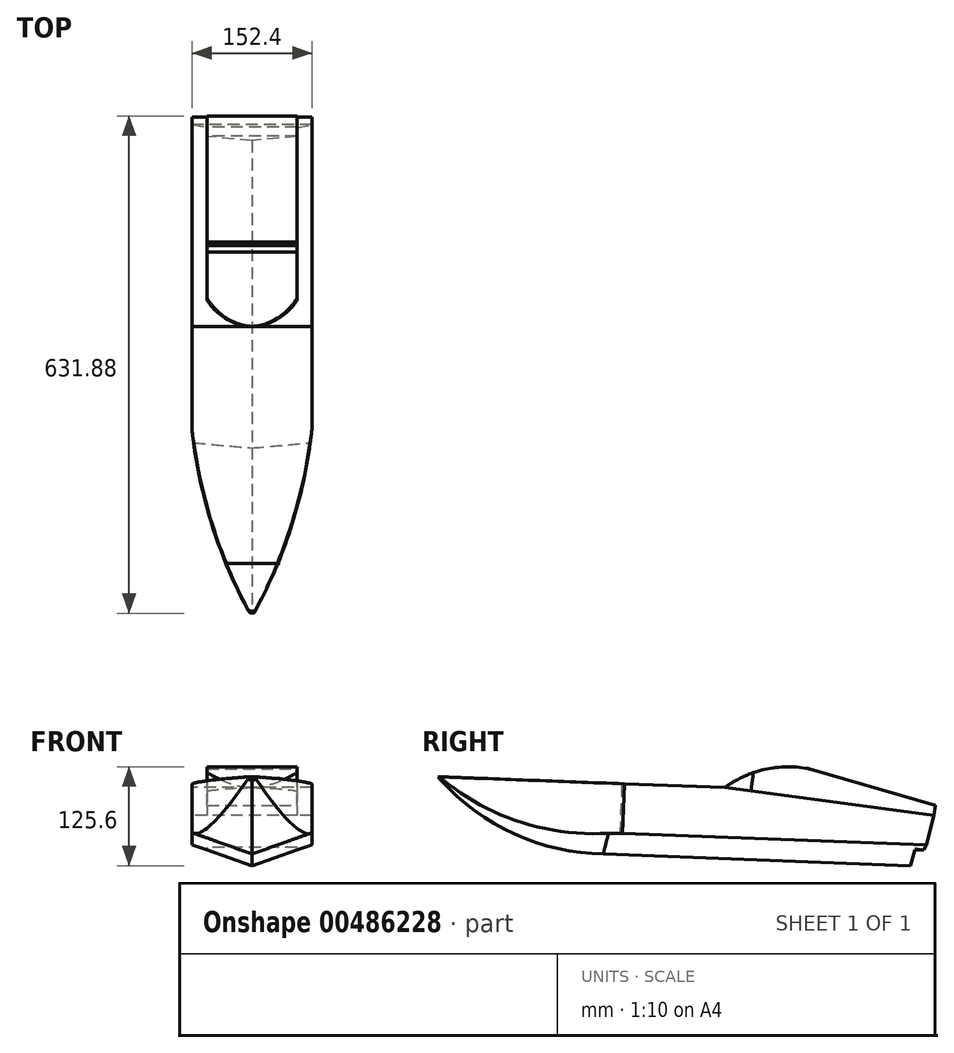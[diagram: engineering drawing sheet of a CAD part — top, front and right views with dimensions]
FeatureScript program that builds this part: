
annotation { "Feature Type Name" : "Feature", "Feature Type Description" : "" }
export const myFeature = defineFeature(function(context is Context, id is Id, definition is map)
    precondition{}
    {
        {
            var Q0;
            Q0=qCreatedBy(makeId("Right.planeOp"),FACE);
            var sketch = newSketch(context, id + "F0", { "sketchPlane" : qUnion([Q0])});
            skLineSegment(sketch, "E0", {"start": v(-294.84, 31.95) * mm, "end": v(70.05, 18.1) * mm});
            skLineSegment(sketch, "E1", {"start": v(70.05, 18.1) * mm, "end": v(335.9, -17.4) * mm});
            skLineSegment(sketch, "E2", {"start": v(335.9, -17.4) * mm, "end": v(326.2, -54.44) * mm});
            skLineSegment(sketch, "E3", {"start": v(326.2, -54.44) * mm, "end": v(73.83, -35.78) * mm});
            skArc(sketch, "E4", {"start": v(-294.84, 31.95) * mm, "mid": v(-201.79, -39.18) * mm, "end": v(-87.88, -66.47) * mm});
            skArc(sketch, "E5", {"start": v(-281.12, 17.08) * mm, "mid": v(-104.62, -15.92) * mm, "end": v(73.83, -35.78) * mm});
            skLineSegment(sketch, "E6", {"start": v(-87.88, -66.47) * mm, "end": v(312.96, -81.69) * mm});
            skLineSegment(sketch, "E7", {"start": v(326.2, -54.44) * mm, "end": v(312.96, -81.69) * mm});
            skLineSegment(sketch, "E8", {"start": v(-294.84, 31.95) * mm, "end": v(-379.88, 131.03) * mm});
            skLineSegment(sketch, "E9", {"start": v(-379.88, 131.03) * mm, "end": v(-230.86, 29.52) * mm});
            skSolve(sketch);
        }
        {
            var Q0;
            Q0 = qSketchRegion(id + "F0", true);
            extrude(context, id + "F1", {"entities" : qUnion([Q0]), "depth" : 152.4 * mm, "offsetDistance" : 25.4 * mm});
        }
        {
            var Q0;
            Q0=makeQuery(id+"F1.opExtrude","SWEPT_FACE",FACE,{"disambiguationData":[OSD([sQuery(id+"F0.wireOp",EDGE,"E2")])]});
            var sketch = newSketch(context, id + "F2", { "sketchPlane" : qUnion([Q0])});
            skLineSegment(sketch, "E10", {"start": v(-76.2, 29.96) * mm, "end": v(-76.2, 11.3) * mm, "construction": true});
            skLineSegment(sketch, "E11", {"start": v(-76.2, 11.3) * mm, "end": v(-76.2, 7.51) * mm, "construction": true});
            skLineSegment(sketch, "E12", {"start": v(0, 7.51) * mm, "end": v(0, 29.96) * mm});
            skLineSegment(sketch, "E13", {"start": v(-152.4, 29.96) * mm, "end": v(-76.2, 29.96) * mm});
            skLineSegment(sketch, "E14", {"start": v(0, 29.96) * mm, "end": v(-76.2, 29.96) * mm});
            skLineSegment(sketch, "E15", {"start": v(-76.2, 29.96) * mm, "end": v(-76.2, 7.51) * mm});
            skLineSegment(sketch, "E16", {"start": v(0, 29.96) * mm, "end": v(0, 18.74) * mm});
            skLineSegment(sketch, "E17", {"start": v(0, 29.96) * mm, "end": v(45.97, -2.77) * mm});
            skLineSegment(sketch, "E18", {"start": v(45.97, -2.77) * mm, "end": v(-180.85, -2.77) * mm});
            skLineSegment(sketch, "E19", {"start": v(-180.85, -2.77) * mm, "end": v(-152.4, 29.96) * mm});
            skLineSegment(sketch, "E20", {"start": v(-180.85, -2.77) * mm, "end": v(-273.96, -108.66) * mm});
            skLineSegment(sketch, "E21", {"start": v(-273.96, -108.66) * mm, "end": v(130.47, -108.66) * mm});
            skLineSegment(sketch, "E22", {"start": v(130.47, -108.66) * mm, "end": v(45.97, -2.77) * mm});
            skLineSegment(sketch, "E23", {"start": v(-152.4, 29.96) * mm, "end": v(-76.2, 1.98) * mm});
            skLineSegment(sketch, "E24", {"start": v(-76.2, 1.98) * mm, "end": v(0, 29.96) * mm});
            skSolve(sketch);
        }
        {
            var Q0;
            Q0=makeQuery(id+"F1.opExtrude","CAP_FACE",FACE,{"disambiguationData":[OSD([sQuery(id+"F0.wireOp",EDGE,"E0"),sQuery(id+"F0.wireOp",EDGE,"E1"),sQuery(id+"F0.wireOp",EDGE,"E2"),sQuery(id+"F0.wireOp",EDGE,"E4"),sQuery(id+"F0.wireOp",EDGE,"E6"),sQuery(id+"F0.wireOp",EDGE,"E7")])],"isStart":true});
            var sketch = newSketch(context, id + "F3", { "sketchPlane" : qUnion([Q0])});
            skLineSegment(sketch, "E25", {"start": v(-326.2, -54.44) * mm, "end": v(-60.2, -32.43) * mm});
            skArc(sketch, "E26", {"start": v(-60.2, -32.43) * mm, "mid": v(114.76, -14.87) * mm, "end": v(286.54, 22.7) * mm});
            skLineSegment(sketch, "E27", {"start": v(286.54, 22.7) * mm, "end": v(364.94, 59.76) * mm});
            skSolve(sketch);
        }
        {
            var Q0;
            Q0=makeQuery(id+"F2.imprint","IMPRINT",FACE,{"disambiguationData":[TD([[makeQuery(id+"F2.imprint","IMPRINT",EDGE,{"derivedFrom":sQuery(id+"F2.wireOp",EDGE,"E17")}),-1.0]])]});
            var Q1;
            Q1=makeQuery(id+"F2.imprint","IMPRINT",FACE,{"disambiguationData":[TD([[makeQuery(id+"F2.imprint","IMPRINT",EDGE,{"derivedFrom":sQuery(id+"F2.wireOp",EDGE,"E18")}),1.0]])]});
            var Q2;
            Q2=makeQuery(id+"F1.opExtrude","CAP_EDGE",EDGE,{"disambiguationData":[OSD([sQuery(id+"F0.wireOp",EDGE,"E8")])],"isStart":false});
            var Q3;
            Q3=makeQuery(id+"F1.opExtrude","CAP_EDGE",EDGE,{"disambiguationData":[OSD([sQuery(id+"F0.wireOp",EDGE,"E4")])],"isStart":false});
            var Q4;
            Q4=makeQuery(id+"F1.opExtrude","CAP_EDGE",EDGE,{"disambiguationData":[OSD([sQuery(id+"F0.wireOp",EDGE,"E6")])],"isStart":false});
            sweep(context, id + "F4", {"operationType" : NewBodyOperationType.REMOVE, "profiles" : qUnion([Q0, Q1]), "path" : qUnion([Q2, Q3, Q4])});
        }
        {
            var Q0;
            Q0=makeQuery(id+"F1.opExtrude","CAP_FACE",FACE,{"disambiguationData":[OSD([sQuery(id+"F0.wireOp",EDGE,"E0"),sQuery(id+"F0.wireOp",EDGE,"E1"),sQuery(id+"F0.wireOp",EDGE,"E2"),sQuery(id+"F0.wireOp",EDGE,"E4"),sQuery(id+"F0.wireOp",EDGE,"E6"),sQuery(id+"F0.wireOp",EDGE,"E7")])],"isStart":false});
            var sketch = newSketch(context, id + "F5", { "sketchPlane" : qUnion([Q0])});
            skArc(sketch, "E28", {"start": v(-386.63, 122.11) * mm, "mid": v(-246.1, 14.63) * mm, "end": v(-77.53, -39.12) * mm});
            skLineSegment(sketch, "E29", {"start": v(-230.86, 29.52) * mm, "end": v(-280, 33.98) * mm});
            skLineSegment(sketch, "E30", {"start": v(-280, 33.98) * mm, "end": v(-230.86, 29.52) * mm});
            skLineSegment(sketch, "E31", {"start": v(-230.86, 29.52) * mm, "end": v(-226.23, 151.46) * mm});
            skLineSegment(sketch, "E32", {"start": v(-226.23, 151.46) * mm, "end": v(-406.8, 151.46) * mm});
            skLineSegment(sketch, "E33", {"start": v(-406.8, 151.46) * mm, "end": v(-386.63, 122.11) * mm});
            skLineSegment(sketch, "E34", {"start": v(-280, 33.98) * mm, "end": v(-323.7, 40.75) * mm});
            skLineSegment(sketch, "E35", {"start": v(-323.7, 40.75) * mm, "end": v(-320.42, 61.87) * mm});
            skSolve(sketch);
        }
        {
            var Q0;
            Q0 = qSketchRegion(id + "F5", true);
            extrude(context, id + "F6", {"entities" : qUnion([Q0]), "operationType" : NewBodyOperationType.REMOVE, "oppositeDirection" : true, "depth" : 584.2 * mm, "offsetDistance" : 25.4 * mm});
        }
        {
            var Q0;
            Q0=makeQuery(id+"F1.opExtrude","SWEPT_FACE",FACE,{"disambiguationData":[OSD([sQuery(id+"F0.wireOp",EDGE,"E0")])]});
            var sketch = newSketch(context, id + "F7", { "sketchPlane" : qUnion([Q0])});
            skArc(sketch, "E36", {"start": v(76.04, -299.98) * mm, "mid": v(126.16, -182.86) * mm, "end": v(152.4, -58.2) * mm});
            skLineSegment(sketch, "E37", {"start": v(76.04, -299.98) * mm, "end": v(76.04, -160.68) * mm, "construction": true});
            skArc(sketch, "E38.MirrorCS", {"start": v(76.04, -299.98) * mm, "mid": v(25.92, -182.86) * mm, "end": v(-0.32, -58.2) * mm});
            skLineSegment(sketch, "E39", {"start": v(152.4, -58.2) * mm, "end": v(161.27, -70.32) * mm});
            skLineSegment(sketch, "E40", {"start": v(152.4, -58.2) * mm, "end": v(307.31, -259.52) * mm});
            skLineSegment(sketch, "E41", {"start": v(307.31, -259.52) * mm, "end": v(76.04, -299.98) * mm});
            skLineSegment(sketch, "E42", {"start": v(76.04, -299.98) * mm, "end": v(-128.98, -291.66) * mm});
            skLineSegment(sketch, "E43", {"start": v(-128.98, -291.66) * mm, "end": v(-0.32, -58.2) * mm});
            skSolve(sketch);
        }
        {
            var Q0;
            Q0 = qSketchRegion(id + "F7", true);
            extrude(context, id + "F8", {"entities" : qUnion([Q0]), "operationType" : NewBodyOperationType.REMOVE, "oppositeDirection" : true, "depth" : 508 * mm, "offsetDistance" : 25.4 * mm});
        }
        {
            var Q0;
            Q0=makeQuery(id+"F8.boolean.opBoolean","COPY",FACE,{"derivedFrom":makeQuery(id+"F8.opExtrude","CAP_FACE",FACE,{"disambiguationData":[OSD([sQuery(id+"F7.wireOp",EDGE,"E38.MirrorCS"),sQuery(id+"F7.wireOp",EDGE,"E42"),sQuery(id+"F7.wireOp",EDGE,"E43")])],"isStart":true})});
            var sketch = newSketch(context, id + "F9", { "sketchPlane" : qUnion([Q0])});
            skLineSegment(sketch, "E44", {"start": v(72.52, 293.48) * mm, "end": v(43.58, 231.82) * mm});
            skLineSegment(sketch, "E45", {"start": v(43.58, 231.82) * mm, "end": v(0, 231.82) * mm});
            skLineSegment(sketch, "E46", {"start": v(0, 231.82) * mm, "end": v(0, 256.53) * mm});
            skLineSegment(sketch, "E47", {"start": v(0, 256.53) * mm, "end": v(72.52, 293.48) * mm});
            skLineSegment(sketch, "E48", {"start": v(72.52, 293.48) * mm, "end": v(76.24, 300.45) * mm});
            skLineSegment(sketch, "E49", {"start": v(76.24, 300.45) * mm, "end": v(-6.26, 271.44) * mm});
            skLineSegment(sketch, "E50", {"start": v(-6.26, 271.44) * mm, "end": v(0, 256.53) * mm});
            skLineSegment(sketch, "E51", {"start": v(76.24, 300.45) * mm, "end": v(78.77, 270) * mm, "construction": true});
            skLineSegment(sketch, "E52.MirrorCS", {"start": v(80.34, 292.4) * mm, "end": v(8.38, 242.7) * mm});
            skLineSegment(sketch, "E53.MirrorCS", {"start": v(158.69, 269.71) * mm, "end": v(81.07, 294.2) * mm});
            skLineSegment(sketch, "E54.MirrorCS", {"start": v(76.24, 300.45) * mm, "end": v(162.4, 285.45) * mm});
            skLineSegment(sketch, "E55.MirrorCS", {"start": v(162.4, 285.45) * mm, "end": v(158.69, 269.71) * mm});
            skLineSegment(sketch, "E56.MirrorCS", {"start": v(162.77, 245.34) * mm, "end": v(158.69, 269.71) * mm});
            skLineSegment(sketch, "E57.MirrorCS", {"start": v(119.79, 238.15) * mm, "end": v(162.77, 245.34) * mm});
            skLineSegment(sketch, "E58", {"start": v(43.58, 231.82) * mm, "end": v(72.52, 293.48) * mm});
            skLineSegment(sketch, "E59", {"start": v(111.81, 231.82) * mm, "end": v(80.34, 292.4) * mm});
            skLineSegment(sketch, "E60", {"start": v(111.81, 231.82) * mm, "end": v(152.94, 231.82) * mm});
            skLineSegment(sketch, "E61", {"start": v(152.94, 231.82) * mm, "end": v(162.77, 245.34) * mm});
            skSolve(sketch);
        }
        {
            var Q0;
            Q0 = qSketchRegion(id + "F9", true);
            extrude(context, id + "F10", {"entities" : qUnion([Q0]), "operationType" : NewBodyOperationType.REMOVE, "oppositeDirection" : true, "depth" : 25.4 * mm, "offsetDistance" : 25.4 * mm});
        }
        {
            var Q0;
            Q0=makeQuery(id+"F3.imprint","IMPRINT",FACE,{"disambiguationData":[TD([[makeQuery(id+"F3.imprint","IMPRINT",EDGE,{"derivedFrom":sQuery(id+"F3.wireOp",EDGE,"E25")}),1.0]])]});
            var sketch = newSketch(context, id + "F11", { "sketchPlane" : qUnion([Q0])});
            skLineSegment(sketch, "E62", {"start": v(290.8, 35.33) * mm, "end": v(291.1, 32.1) * mm});
            skLineSegment(sketch, "E63", {"start": v(231.53, 29.94) * mm, "end": v(294.75, 43.82) * mm});
            skLineSegment(sketch, "E64", {"start": v(294.75, 43.82) * mm, "end": v(290.8, 35.33) * mm});
            skLineSegment(sketch, "E65", {"start": v(231.06, 29.5) * mm, "end": v(291.8, 31.83) * mm});
            skLineSegment(sketch, "E66", {"start": v(291.8, 31.83) * mm, "end": v(292.78, 39.57) * mm});
            skLineSegment(sketch, "E67", {"start": v(292.78, 39.57) * mm, "end": v(231.53, 30.54) * mm});
            skLineSegment(sketch, "E68", {"start": v(231.53, 30.54) * mm, "end": v(231.06, 29.5) * mm});
            skSolve(sketch);
        }
        {
            var Q0;
            Q0 = qSketchRegion(id + "F11", true);
            extrude(context, id + "F12", {"entities" : qUnion([Q0]), "operationType" : NewBodyOperationType.REMOVE, "oppositeDirection" : true, "depth" : 508 * mm, "offsetDistance" : 25.4 * mm});
        }
        {
            var Q0;
            Q0=makeQuery(id+"F1.opExtrude","SWEPT_FACE",FACE,{"disambiguationData":[OSD([sQuery(id+"F0.wireOp",EDGE,"E1")])]});
            var sketch = newSketch(context, id + "F13", { "sketchPlane" : qUnion([Q0])});
            skLineSegment(sketch, "E69", {"start": v(76.2, 67.03) * mm, "end": v(76.2, 335.25) * mm, "construction": true});
            skLineSegment(sketch, "E70", {"start": v(152.4, 201.14) * mm, "end": v(0, 201.14) * mm, "construction": true});
            skLineSegment(sketch, "E71", {"start": v(0, 201.14) * mm, "end": v(76.2, 201.14) * mm, "construction": true});
            skLineSegment(sketch, "E72", {"start": v(76.2, 201.14) * mm, "end": v(38.1, 201.14) * mm, "construction": true});
            skLineSegment(sketch, "E73", {"start": v(38.1, 201.14) * mm, "end": v(0, 201.14) * mm, "construction": true});
            skLineSegment(sketch, "E74", {"start": v(19.05, 201.14) * mm, "end": v(19.05, 335.25) * mm, "construction": true});
            skLineSegment(sketch, "E75", {"start": v(19.05, 335.25) * mm, "end": v(19.05, 67.03) * mm, "construction": true});
            skLineSegment(sketch, "E76", {"start": v(19.05, 67.03) * mm, "end": v(19.05, 201.14) * mm, "construction": true});
            skLineSegment(sketch, "E77", {"start": v(19.05, 134.09) * mm, "end": v(19.05, 67.03) * mm, "construction": true});
            skArc(sketch, "E78", {"start": v(19.05, 100.56) * mm, "mid": v(43.53, 76.8) * mm, "end": v(76.2, 67.03) * mm});
            skLineSegment(sketch, "E79", {"start": v(76.2, 335.25) * mm, "end": v(19.05, 335.25) * mm, "construction": true});
            skLineSegment(sketch, "E80", {"start": v(19.05, 100.56) * mm, "end": v(19.05, 335.25) * mm});
            skArc(sketch, "E81.MirrorCS", {"start": v(133.35, 100.56) * mm, "mid": v(108.87, 76.8) * mm, "end": v(76.2, 67.03) * mm});
            skLineSegment(sketch, "E82", {"start": v(133.35, 100.56) * mm, "end": v(133.35, 335.25) * mm});
            skLineSegment(sketch, "E83", {"start": v(133.35, 335.25) * mm, "end": v(19.05, 335.25) * mm});
            skSolve(sketch);
        }
        {
            var Q0;
            Q0 = qSketchRegion(id + "F13", true);
            extrude(context, id + "F14", {"entities" : qUnion([Q0]), "operationType" : NewBodyOperationType.ADD, "depth" : 38.1 * mm, "offsetDistance" : 25.4 * mm});
        }
        {
            var Q0;
            {var subQ0=sQuery(id+"F0.wireOp",EDGE,"E7");var subQ2=sQuery(id+"F0.wireOp",EDGE,"E2");var subQ4=sQuery(id+"F0.wireOp",EDGE,"E1");var subQ6=sQuery(id+"F0.wireOp",EDGE,"E0");var subQ7=makeQuery(id+"F1.opExtrude","SWEPT_FACE",FACE,{"disambiguationData":[OSD([subQ6])]});var subQ9=sQuery(id+"F0.wireOp",EDGE,"E6");var subQ11=sQuery(id+"F0.wireOp",EDGE,"E9");var subQ12=sQuery(id+"F0.wireOp",EDGE,"E4");var subQ13=sQuery(id+"F0.wireOp",EDGE,"E8");Q0=makeQuery(id+"F8.boolean.opBoolean","SPLIT",FACE,{"disambiguationData":[TD([subQ7])],"derivedFrom":makeQuery(id+"F4.boolean.opBoolean","SPLIT",FACE,{"disambiguationData":[TD([subQ7])],"derivedFrom":makeQuery(id+"F1.opExtrude","CAP_FACE",FACE,{"disambiguationData":[OSD([subQ6,subQ4,subQ2,subQ12,subQ9,subQ0,subQ13,subQ11])],"isStart":false})})});}
            var sketch = newSketch(context, id + "F15", { "sketchPlane" : qUnion([Q0])});
            skArc(sketch, "E84", {"start": v(177.35, 42) * mm, "mid": v(121.19, 41.33) * mm, "end": v(70.05, 18.1) * mm});
            skLineSegment(sketch, "E85", {"start": v(335.9, -17.4) * mm, "end": v(362.3, 53.01) * mm});
            skLineSegment(sketch, "E86", {"start": v(362.3, 53.01) * mm, "end": v(76.16, 93.33) * mm});
            skLineSegment(sketch, "E87", {"start": v(76.16, 93.33) * mm, "end": v(70.05, 18.1) * mm});
            skLineSegment(sketch, "E88", {"start": v(177.35, 42) * mm, "end": v(340.37, -5.5) * mm});
            skSolve(sketch);
        }
        {
            var Q0;
            Q0 = qSketchRegion(id + "F15", true);
            extrude(context, id + "F16", {"entities" : qUnion([Q0]), "operationType" : NewBodyOperationType.REMOVE, "oppositeDirection" : true, "depth" : 508 * mm, "offsetDistance" : 25.4 * mm});
        }
        {
            var Q0;
            Q0=makeQuery(id+"F1.opExtrude","SWEPT_FACE",FACE,{"disambiguationData":[OSD([sQuery(id+"F0.wireOp",EDGE,"E2")])]});
            var sketch = newSketch(context, id + "F17", { "sketchPlane" : qUnion([Q0])});
            skLineSegment(sketch, "E89", {"start": v(-152.4, 29.96) * mm, "end": v(0, 29.96) * mm, "construction": true});
            skLineSegment(sketch, "E90", {"start": v(0, 29.96) * mm, "end": v(-76.2, 29.96) * mm, "construction": true});
            skLineSegment(sketch, "E91", {"start": v(-76.2, 29.96) * mm, "end": v(-38.1, 29.96) * mm, "construction": true});
            skLineSegment(sketch, "E92", {"start": v(-38.1, 29.96) * mm, "end": v(0, 29.96) * mm, "construction": true});
            skLineSegment(sketch, "E93", {"start": v(-19.05, 29.96) * mm, "end": v(-19.05, 0) * mm});
            skLineSegment(sketch, "E94", {"start": v(-152.4, 29.96) * mm, "end": v(-76.2, 29.96) * mm, "construction": true});
            skLineSegment(sketch, "E95", {"start": v(-114.3, 29.96) * mm, "end": v(-152.4, 29.96) * mm, "construction": true});
            skLineSegment(sketch, "E96", {"start": v(-133.35, 29.96) * mm, "end": v(-133.35, 0) * mm});
            skLineSegment(sketch, "E97", {"start": v(-133.35, 0) * mm, "end": v(-19.05, 0) * mm});
            skLineSegment(sketch, "E98", {"start": v(-133.35, 23.03) * mm, "end": v(-19.05, 23.03) * mm});
            skLineSegment(sketch, "E99", {"start": v(-133.35, 0) * mm, "end": v(-34.62, -14.68) * mm});
            skLineSegment(sketch, "E100", {"start": v(-34.62, -14.68) * mm, "end": v(-19.05, 0) * mm});
            skSolve(sketch);
        }
        {
            var Q0;
            {var subQ0=sQuery(id+"F17.wireOp",EDGE,"E97");Q0=makeQuery(id+"F17.imprint","IMPRINT",FACE,{"disambiguationData":[TD([[makeQuery(id+"F17.imprint","IMPRINT",EDGE,{"derivedFrom":subQ0}),1.0]])]});}
            var Q1;
            Q1=makeQuery(id+"F17.imprint","IMPRINT",FACE,{"disambiguationData":[TD([[makeQuery(id+"F17.imprint","IMPRINT",EDGE,{"derivedFrom":sQuery(id+"F17.wireOp",EDGE,"E97")}),-1.0]])]});
            extrude(context, id + "F18", {"entities" : qUnion([Q0, Q1]), "operationType" : NewBodyOperationType.REMOVE, "oppositeDirection" : true, "depth" : 12.7 * mm, "offsetDistance" : 25.4 * mm});
        }
    });
